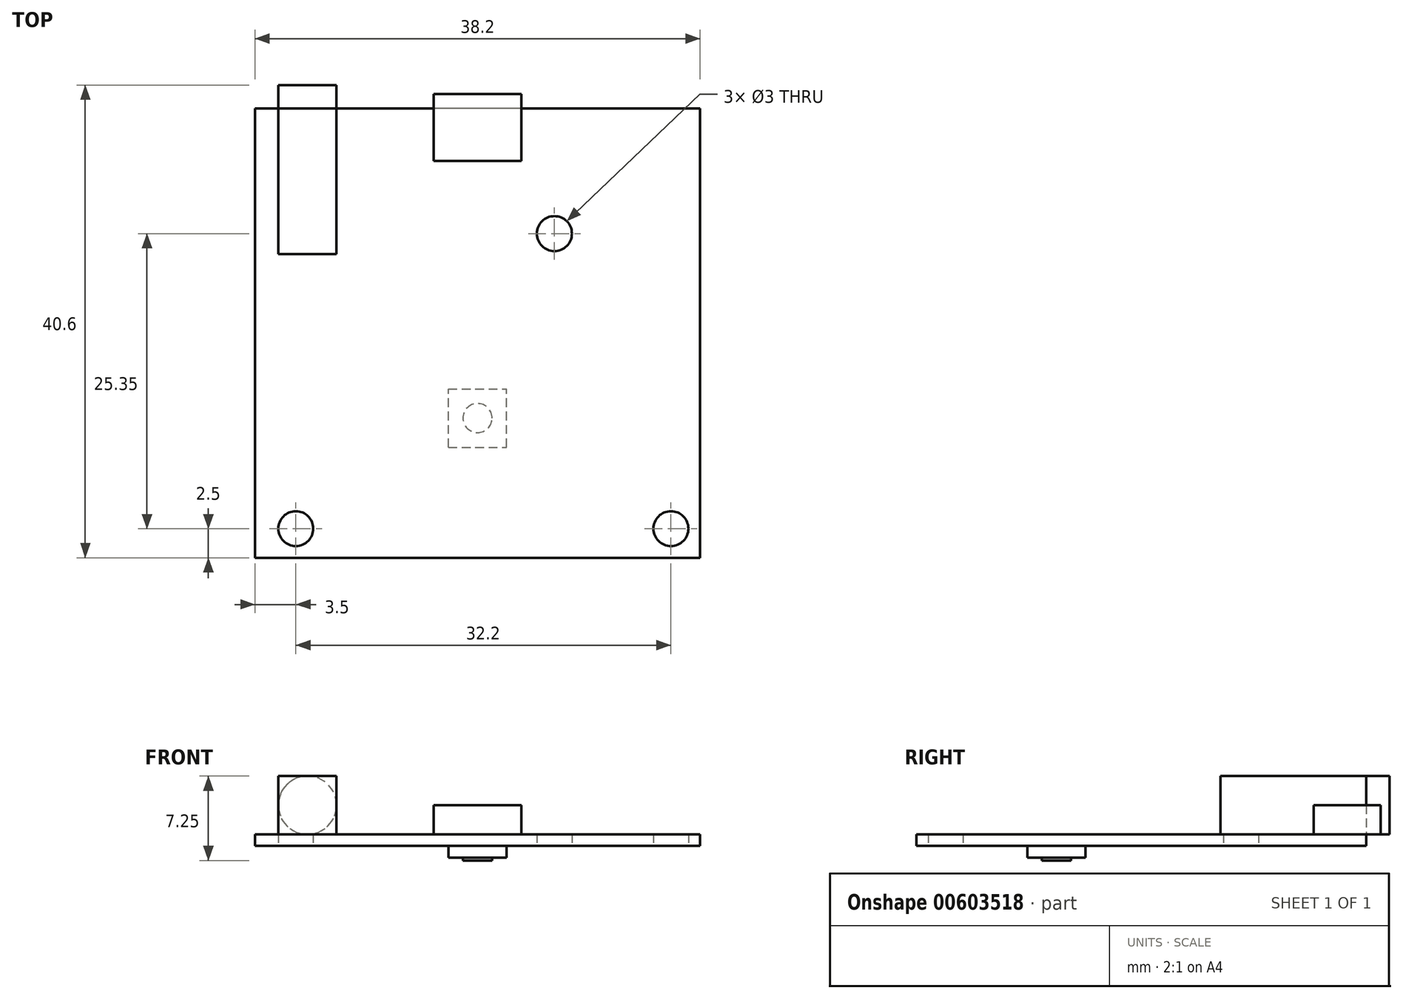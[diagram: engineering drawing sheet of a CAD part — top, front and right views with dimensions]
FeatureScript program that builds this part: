
annotation { "Feature Type Name" : "Feature", "Feature Type Description" : "" }
export const myFeature = defineFeature(function(context is Context, id is Id, definition is map)
    precondition{}
    {
        {
            var Q0;
            Q0=qCreatedBy(makeId("Top.planeOp"),FACE);
            var sketch = newSketch(context, id + "F0", { "sketchPlane" : qUnion([Q0])});
            skLineSegment(sketch, "E0.bottom", {"start": v(19.1, -19.3) * mm, "end": v(-19.1, -19.3) * mm});
            skLineSegment(sketch, "E0.top", {"start": v(19.1, 19.3) * mm, "end": v(-19.1, 19.3) * mm});
            skLineSegment(sketch, "E0.left", {"start": v(19.1, -19.3) * mm, "end": v(19.1, 19.3) * mm});
            skLineSegment(sketch, "E0.right", {"start": v(-19.1, -19.3) * mm, "end": v(-19.1, 19.3) * mm});
            skPoint(sketch, "E0.middle", {"position": v(0, 0) * mm});
            skCircle(sketch, "E1", {"center": v(-15.6, -16.8) * mm, "radius": 1.5 * mm});
            skCircle(sketch, "E2", {"center": v(16.6, -16.8) * mm, "radius": 1.5 * mm});
            skCircle(sketch, "E3", {"center": v(6.6, 8.55) * mm, "radius": 1.5 * mm});
            skLineSegment(sketch, "E4", {"start": v(-15.6, -16.8) * mm, "end": v(16.6, -16.8) * mm, "construction": true});
            skSolve(sketch);
        }
        {
            var Q0;
            Q0=makeQuery(id+"F0.imprint","IMPRINT",FACE,{"disambiguationData":[TD([[makeQuery(id+"F0.imprint","IMPRINT",EDGE,{"derivedFrom":sQuery(id+"F0.wireOp",EDGE,"E0.bottom")}),-1.0]])]});
            extrude(context, id + "F1", {"entities" : qUnion([Q0]), "depth" : 1 * mm, "offsetDistance" : 25 * mm});
        }
        {
            var Q0;
            Q0=makeQuery(id+"F1.opExtrude","CAP_FACE",FACE,{"disambiguationData":[OSD([sQuery(id+"F0.wireOp",EDGE,"E0.bottom"),sQuery(id+"F0.wireOp",EDGE,"E0.top"),sQuery(id+"F0.wireOp",EDGE,"E0.left"),sQuery(id+"F0.wireOp",EDGE,"E0.right"),sQuery(id+"F0.wireOp",EDGE,"E1"),sQuery(id+"F0.wireOp",EDGE,"E2"),sQuery(id+"F0.wireOp",EDGE,"E3")])],"isStart":false});
            var sketch = newSketch(context, id + "F2", { "sketchPlane" : qUnion([Q0])});
            skLineSegment(sketch, "E5.bottom", {"start": v(3.75, 14.8) * mm, "end": v(-3.75, 14.8) * mm});
            skLineSegment(sketch, "E5.top", {"start": v(3.75, 20.55) * mm, "end": v(-3.75, 20.55) * mm});
            skLineSegment(sketch, "E5.left", {"start": v(3.75, 14.8) * mm, "end": v(3.75, 20.55) * mm});
            skLineSegment(sketch, "E5.right", {"start": v(-3.75, 14.8) * mm, "end": v(-3.75, 20.55) * mm});
            skPoint(sketch, "E5.middle", {"position": v(0, 17.68) * mm});
            skSolve(sketch);
        }
        {
            var Q0;
            {var subQ0=sQuery(id+"F2.wireOp",EDGE,"E5.bottom");Q0=makeQuery(id+"F2.imprint","IMPRINT",FACE,{"disambiguationData":[TD([[makeQuery(id+"F2.imprint","IMPRINT",EDGE,{"derivedFrom":subQ0}),-1.0]])]});}
            var Q1;
            {var subQ0=sQuery(id+"F2.wireOp",EDGE,"E5.top");Q1=makeQuery(id+"F2.imprint","IMPRINT",FACE,{"disambiguationData":[TD([[makeQuery(id+"F2.imprint","IMPRINT",EDGE,{"derivedFrom":subQ0}),1.0]])]});}
            extrude(context, id + "F3", {"entities" : qUnion([Q0, Q1]), "operationType" : NewBodyOperationType.ADD, "depth" : 2.5 * mm, "offsetDistance" : 25 * mm});
        }
        {
            var Q0;
            Q0=makeQuery(id+"F1.opExtrude","CAP_FACE",FACE,{"disambiguationData":[OSD([sQuery(id+"F0.wireOp",EDGE,"E0.bottom"),sQuery(id+"F0.wireOp",EDGE,"E0.top"),sQuery(id+"F0.wireOp",EDGE,"E0.left"),sQuery(id+"F0.wireOp",EDGE,"E0.right"),sQuery(id+"F0.wireOp",EDGE,"E1"),sQuery(id+"F0.wireOp",EDGE,"E2"),sQuery(id+"F0.wireOp",EDGE,"E3")])],"isStart":true});
            var sketch = newSketch(context, id + "F4", { "sketchPlane" : qUnion([Q0])});
            skLineSegment(sketch, "E6.bottom", {"start": v(-2.5, 9.8) * mm, "end": v(2.5, 9.8) * mm});
            skLineSegment(sketch, "E6.top", {"start": v(-2.5, 4.8) * mm, "end": v(2.5, 4.8) * mm});
            skLineSegment(sketch, "E6.left", {"start": v(-2.5, 9.8) * mm, "end": v(-2.5, 4.8) * mm});
            skLineSegment(sketch, "E6.right", {"start": v(2.5, 9.8) * mm, "end": v(2.5, 4.8) * mm});
            skPoint(sketch, "E6.middle", {"position": v(0, 7.3) * mm});
            skSolve(sketch);
        }
        {
            var Q0;
            Q0=makeQuery(id+"F4.imprint","IMPRINT",FACE,{"disambiguationData":[TD([[makeQuery(id+"F4.imprint","IMPRINT",EDGE,{"derivedFrom":sQuery(id+"F4.wireOp",EDGE,"E6.bottom")}),-1.0]])]});
            extrude(context, id + "F5", {"entities" : qUnion([Q0]), "operationType" : NewBodyOperationType.ADD, "depth" : 1 * mm, "offsetDistance" : 25 * mm});
        }
        {
            var Q0;
            Q0=makeQuery(id+"F5.opExtrude","CAP_FACE",FACE,{"disambiguationData":[OSD([sQuery(id+"F4.wireOp",EDGE,"E6.bottom"),sQuery(id+"F4.wireOp",EDGE,"E6.top"),sQuery(id+"F4.wireOp",EDGE,"E6.left"),sQuery(id+"F4.wireOp",EDGE,"E6.right")])],"isStart":false});
            var sketch = newSketch(context, id + "F6", { "sketchPlane" : qUnion([Q0])});
            skCircle(sketch, "E7", {"center": v(0, 7.3) * mm, "radius": 1.25 * mm});
            skPoint(sketch, "E7.centerSnap0", {"position": v(-2.5, 7.3) * mm});
            skSolve(sketch);
        }
        {
            var Q0;
            Q0=makeQuery(id+"F6.imprint","IMPRINT",FACE,{"disambiguationData":[TD([[makeQuery(id+"F6.imprint","IMPRINT",EDGE,{"derivedFrom":sQuery(id+"F6.wireOp",EDGE,"E7")}),1.0]])]});
            extrude(context, id + "F7", {"entities" : qUnion([Q0]), "operationType" : NewBodyOperationType.ADD, "depth" : 0.25 * mm, "offsetDistance" : 25 * mm});
        }
        {
            var Q0;
            Q0=makeQuery(id+"F1.opExtrude","CAP_FACE",FACE,{"disambiguationData":[OSD([sQuery(id+"F0.wireOp",EDGE,"E0.bottom"),sQuery(id+"F0.wireOp",EDGE,"E0.top"),sQuery(id+"F0.wireOp",EDGE,"E0.left"),sQuery(id+"F0.wireOp",EDGE,"E0.right"),sQuery(id+"F0.wireOp",EDGE,"E1"),sQuery(id+"F0.wireOp",EDGE,"E2"),sQuery(id+"F0.wireOp",EDGE,"E3")])],"isStart":false});
            var sketch = newSketch(context, id + "F8", { "sketchPlane" : qUnion([Q0])});
            skLineSegment(sketch, "E8.bottom", {"start": v(-17.1, 19.3) * mm, "end": v(-12.1, 19.3) * mm});
            skLineSegment(sketch, "E8.top", {"start": v(-17.1, 6.8) * mm, "end": v(-12.1, 6.8) * mm});
            skLineSegment(sketch, "E8.left", {"start": v(-17.1, 19.3) * mm, "end": v(-17.1, 6.8) * mm});
            skLineSegment(sketch, "E8.right", {"start": v(-12.1, 19.3) * mm, "end": v(-12.1, 6.8) * mm});
            skLineSegment(sketch, "E9", {"start": v(-14.6, 19.3) * mm, "end": v(-14.6, 6.8) * mm, "construction": true});
            skSolve(sketch);
        }
        {
            var Q0;
            Q0=makeQuery(id+"F8.imprint","IMPRINT",FACE,{"disambiguationData":[TD([[makeQuery(id+"F8.imprint","IMPRINT",EDGE,{"derivedFrom":sQuery(id+"F8.wireOp",EDGE,"E8.bottom")}),1.0]])]});
            extrude(context, id + "F9", {"entities" : qUnion([Q0]), "operationType" : NewBodyOperationType.ADD, "depth" : 5 * mm, "offsetDistance" : 25 * mm});
        }
        {
            var Q0;
            Q0=makeQuery(id+"F9.boolean.opBoolean","MERGE",FACE,{"derivedFrom":[makeQuery(id+"F1.opExtrude","SWEPT_FACE",FACE,{"disambiguationData":[OSD([sQuery(id+"F0.wireOp",EDGE,"E0.top")])]}),makeQuery(id+"F9.opExtrude","SWEPT_FACE",FACE,{"disambiguationData":[OSD([sQuery(id+"F8.wireOp",EDGE,"E8.bottom")])]})]});
            var sketch = newSketch(context, id + "F10", { "sketchPlane" : qUnion([Q0])});
            skLineSegment(sketch, "E10", {"start": v(17.1, 1) * mm, "end": v(12.1, 1) * mm, "construction": true});
            skLineSegment(sketch, "E11", {"start": v(12.1, 1) * mm, "end": v(17.1, 6) * mm, "construction": true});
            skLineSegment(sketch, "E12", {"start": v(17.1, 1) * mm, "end": v(12.1, 6) * mm, "construction": true});
            skCircle(sketch, "E13", {"center": v(14.6, 3.5) * mm, "radius": 2.5 * mm});
            skSolve(sketch);
        }
        {
            var Q0;
            {var subQ0=sQuery(id+"F10.wireOp",EDGE,"E13");var subQ1=sQuery(id+"F8.wireOp",EDGE,"E8.bottom");var subQ2=makeQuery(id+"F10.imprint","INTERSECT",VERTEX,{"derivedFrom":[makeQuery(id+"F9.opExtrude","CAP_EDGE",EDGE,{"disambiguationData":[OSD([subQ1])],"isStart":false}),subQ0]});Q0=makeQuery(id+"F10.imprint","IMPRINT",FACE,{"disambiguationData":[TD([[makeQuery(id+"F10.imprint","IMPRINT",EDGE,{"disambiguationData":[TD([[subQ2,1.0]])],"derivedFrom":subQ0}),1.0]])]});}
            extrude(context, id + "F11", {"entities" : qUnion([Q0]), "operationType" : NewBodyOperationType.ADD, "depth" : 2 * mm, "offsetDistance" : 25 * mm});
        }
    });
